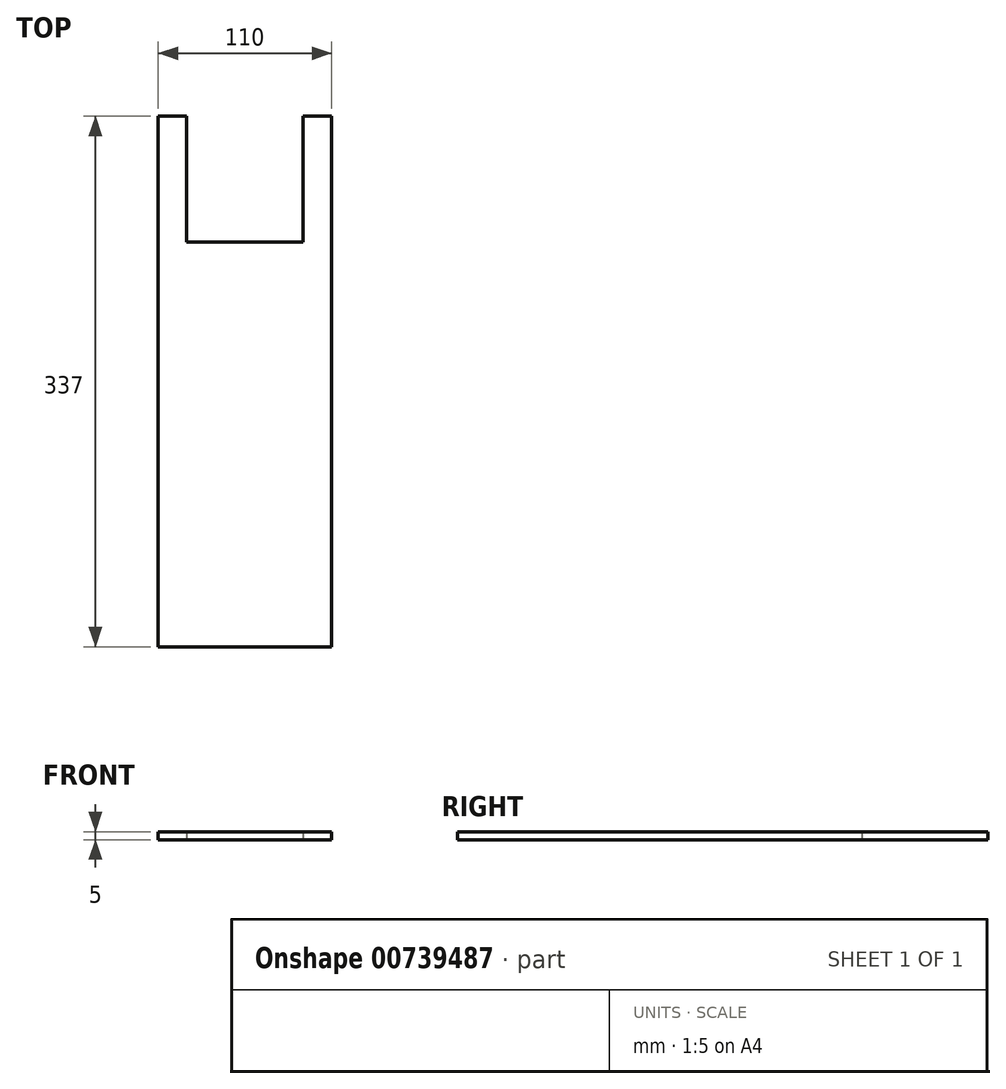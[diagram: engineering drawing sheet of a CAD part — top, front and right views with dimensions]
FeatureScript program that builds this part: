
annotation { "Feature Type Name" : "Feature", "Feature Type Description" : "" }
export const myFeature = defineFeature(function(context is Context, id is Id, definition is map)
    precondition{}
    {
        {
            var Q0;
            Q0=qCreatedBy(makeId("Top.planeOp"),FACE);
            var sketch = newSketch(context, id + "F0", { "sketchPlane" : qUnion([Q0])});
            skLineSegment(sketch, "E0.bottom", {"start": v(55, 168.5) * mm, "end": v(37, 168.5) * mm});
            skLineSegment(sketch, "E0.top", {"start": v(55, -168.5) * mm, "end": v(-55, -168.5) * mm});
            skLineSegment(sketch, "E0.left", {"start": v(55, 168.5) * mm, "end": v(55, -168.5) * mm});
            skLineSegment(sketch, "E0.right", {"start": v(-55, 168.5) * mm, "end": v(-55, -168.5) * mm});
            skPoint(sketch, "E0.middle", {"position": v(0, 0) * mm});
            skLineSegment(sketch, "E1", {"start": v(-55, 168.5) * mm, "end": v(-37, 168.5) * mm});
            skLineSegment(sketch, "E2", {"start": v(-37, 168.5) * mm, "end": v(-37, 88.5) * mm});
            skLineSegment(sketch, "E3", {"start": v(-37, 88.5) * mm, "end": v(37, 88.5) * mm});
            skLineSegment(sketch, "E4", {"start": v(37, 168.5) * mm, "end": v(37, 88.5) * mm});
            skLineSegment(sketch, "E5.trimOffspring", {"start": v(-37, 168.5) * mm, "end": v(-55, 168.5) * mm});
            skSolve(sketch);
        }
        {
            var Q0;
            Q0=makeQuery(id+"F0.imprint","IMPRINT",FACE,{"disambiguationData":[TD([[makeQuery(id+"F0.imprint","IMPRINT",EDGE,{"derivedFrom":sQuery(id+"F0.wireOp",EDGE,"E0.bottom")}),1.0]])]});
            extrude(context, id + "F1", {"entities" : qUnion([Q0]), "depth" : 5 * mm, "offsetDistance" : 25 * mm});
        }
    });
